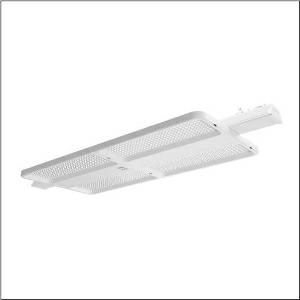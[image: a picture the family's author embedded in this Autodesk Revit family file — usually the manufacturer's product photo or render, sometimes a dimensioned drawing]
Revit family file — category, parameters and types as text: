
# Revit family: highbay_11_fur_licross_r__tragschiene_maxi_51hn11db4mla03_c7ba
name_source: partatom
category: Lighting Fixtures
units: mm (PartAtom-declared; Revit-internal decimal feet)

## family parameters
Cut with Voids When Loaded = No
Host = Face
Light Source = No
Part Type = Normal
Room Calculation Point = No
Round Connector Dimension = Use Diameter
Shared = No

## types (1)
- --- (1 x LED, 30000 lm, 146.5 W, 4000K)
    Apparent Load = 146 VA
    CIE Flux Codes = 85 97 100 100 100
    Color Rendering = 80
    Color Temperature = 4000K
    Default Elevation = 1800 mm
    Description = high bay luminaire Highbay 11 for Licross® trunking rail maxi; direct symmetric narrow distribution, light control with lens of PMMA; UGR ≤ 22 (X = 4H | Y = 8H | S = 0.25H | reflection values 70/50/20); luminous flux: 30.000lm; light colour: 840, colour temperature: 4000K, MacAdam ≤ 2 SDCM (initial), colour rendering: CRI > 80; luminous efficacy: 204,8lm/W; rated service life: 100.000h (L95/B50) at AT= 25°C; control: DALI 2; for wired networking: open and standardized DALI2 interface enables full flexibility and future-proofing for changes in use or functional adaptation through individual programming; multi-sensor luminaire consisting of a DALI2 multi-sensor and DALI2 ECG; multi-sensor luminaire for wired connection to a DALI2 application controller (e.g., SITECO Connect 11 or 21); can also be connected to existing on-site lighting or building automation systems upon request; integrated DALI2 sensor certified according to IEC 62386, Parts 101, 103, 303, and 304; integrated DALI2 ECG provides luminaire data (according to IEC 62386, Part 251), energy data (Part 252), and monitoring and analytics data (Part 253) to higher-level systems for further processing; luminaire with PIR sensor (passive-infrared); with light sensor; luminaire connection: plug, 5-pole, with phase selectionmains connection: 230..240V, AC 50/60Hz; connected load: 146,5W; protection rating (complete): IP64; insulation class (complete): insulation class I (protective earthing); protection symbol: D; certification: CE, ENEC, VDE, UKCA; internal wiring halogen-free; luminaire corresponds to IFS (International Featured Standards) requirements for safety and quality in the food industry; LABS conformity tested according to VDMA 24364:2018-05; housing frame of high-performance plastic PA6, matt traffic white (RAL 9016); cover of PMMA; fixing on rail side of steel, galvanised, white; blank cover of PC/ABS, traffic white (RAL 9016); dimension (LxWxH): 1.250 x 442 x 72mm; permissible operating ambient temperature: -20..+40°C (reducing of maximum allowable ambient temperature of 5°C with ceiling mounting); packaging unit: 1 piece
    Height = 72 mm  [stored 0.23622 ft]
    Lamp = 1 x LED
    Lamp Light Flux = 30000 lm
    Lamp Power = 146.5 W
    Lamp count = 1
    Length = 946 mm
    Luminous efficacy = 205 lm/W
    Manufacturer = Siteco
    ModVariant = No
    Model = 51HN11DB4MLA03
    Mounting Place = Ceiling
    Mounting Type = Pendant
    Number of Poles = 1
    OnlyDefault = Yes
    Power Factor = 1
    Product Name = Highbay 11 für Licross® Tragschiene maxi
    Product group = high bay luminaire
    ProductGroupID = 901
    Protection Class = Protection class I
    Protection Degree = IP 64
    RLX_Detail_Level = 1
    RLX_Emergency_Light_Flux = 0 lm
    RLX_Emergency_Type = 0
    RLX_Emergency_Type_DB = No
    RlxData = <blob elided: 25201 chars, md5=9dbc2242>
    Socket = socket
    Standby Power = 0 W
    System Light Flux = 30000 lm
    System Power = 146 W
    Type Comments = factory setting: luminous flux: 100 % | dim-lin: 254 | 679 mA
    Type Image = l_1363271.jpg
    URL = http://relux.com
    VarID = @adj_012637
    Voltage = 0 V
    Weight = 0.00 kg
    Width = 442 mm

note: [stored X ft] marks values corroborated as IEEE doubles in the binary element streams (Revit-internal decimal feet)

## geometry (parser evidence)
native form markers: Blend x4, Sweep x12
no freeform markers — native parametric forms only
